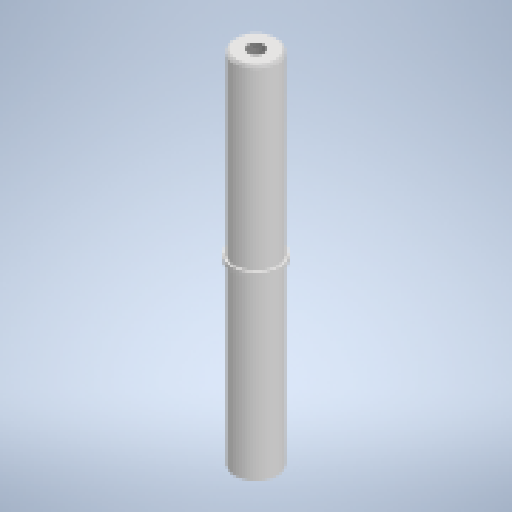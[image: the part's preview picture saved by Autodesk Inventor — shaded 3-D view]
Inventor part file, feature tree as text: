
AUTODESK INVENTOR PART (.ipt)
format: ipt  version: 2024.2 (Build 282272000, 272)  size: 196,608 bytes
history: native  units: mm
features: revolve x1, hole x1, chamfer x1, plane x1, extrude x1, projected_geometry x1
ambient origin geometry x8: Origin, YZ Plane, XZ Plane, XY Plane, X Axis, Y Axis, Z Axis, Center Point
bodies: Solid1 (feature_tree)
feature tree (6):
  revolve  "Revolution1"  Angle=360.0deg
  hole  "Hole1"  [1 undecoded]
  chamfer  "Chamfer1"  Distance=1.0mm Angle=45.0deg
  plane  "Work Plane1"
  extrude  "Extrusion3"  Depth=5.0mm
  projected_geometry  "Projected Loop2"
note: 1 required parameter value undecoded (feature->parameter linkage not recoverable at this tier; creation-order binding heuristic only, values carry confidence <= 0.55)
